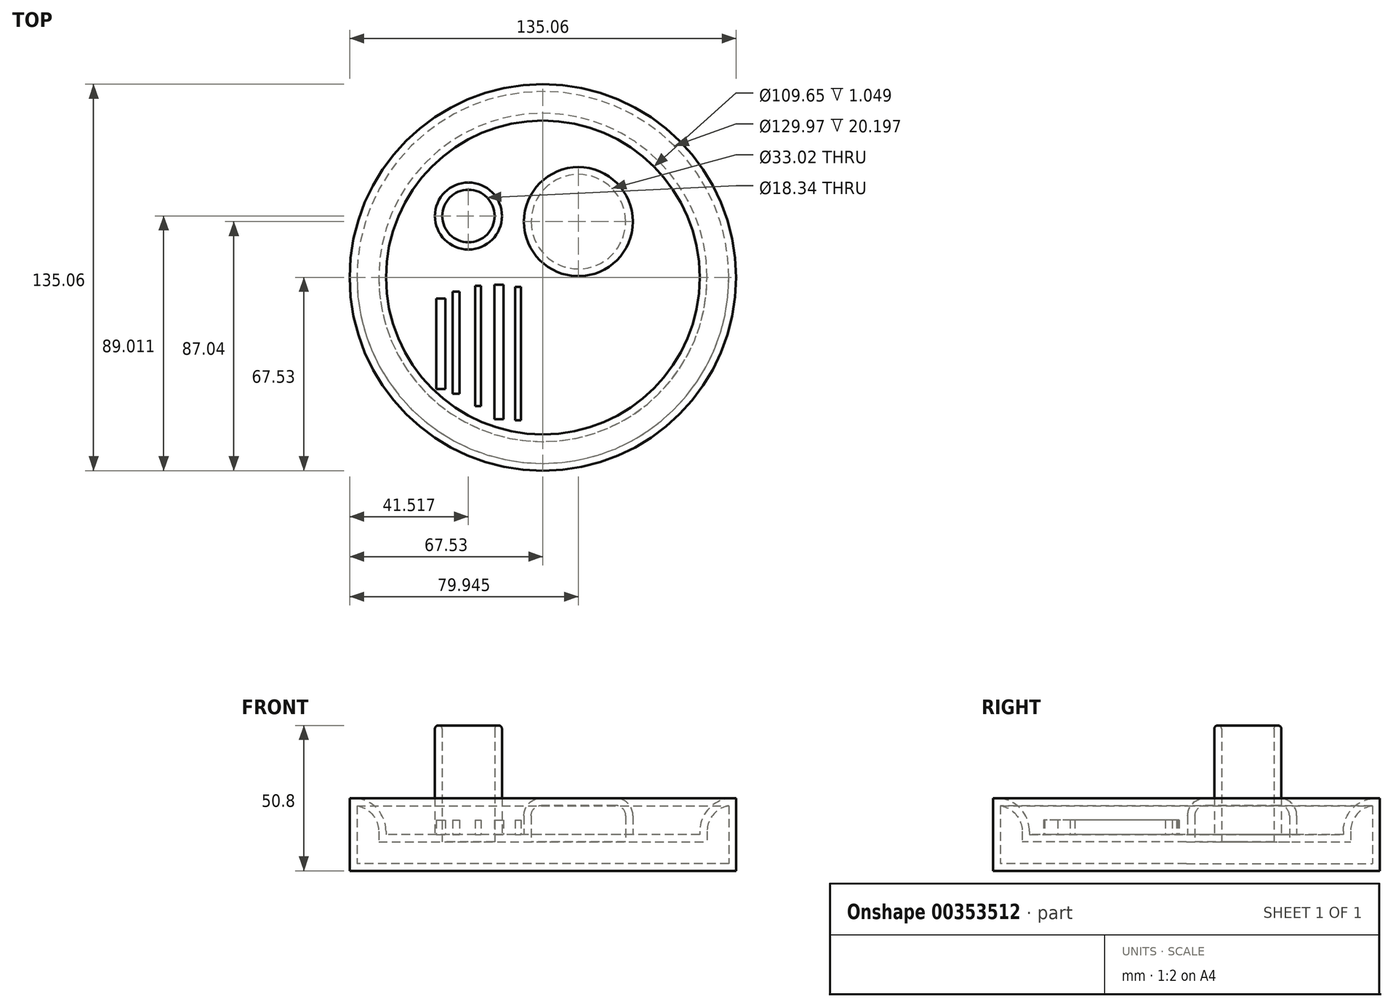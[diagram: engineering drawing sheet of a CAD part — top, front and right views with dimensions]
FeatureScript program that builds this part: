
annotation { "Feature Type Name" : "Feature", "Feature Type Description" : "" }
export const myFeature = defineFeature(function(context is Context, id is Id, definition is map)
    precondition{}
    {
        {
            var Q0;
            Q0=qCreatedBy(makeId("Top.planeOp"),FACE);
            var sketch = newSketch(context, id + "F0", { "sketchPlane" : qUnion([Q0])});
            skCircle(sketch, "E0", {"center": v(0, 0) * mm, "radius": 67.53 * mm});
            skSolve(sketch);
        }
        {
            var Q0;
            Q0=makeQuery(id+"F0.imprint","IMPRINT",FACE,{"disambiguationData":[TD([[makeQuery(id+"F0.imprint","IMPRINT",EDGE,{"derivedFrom":sQuery(id+"F0.wireOp",EDGE,"E0")}),1.0]])]});
            extrude(context, id + "F1", {"entities" : qUnion([Q0]), "depth" : 25.4 * mm});
        }
        {
            var Q0;
            Q0=makeQuery(id+"F1.opExtrude","CAP_FACE",FACE,{"disambiguationData":[OSD([sQuery(id+"F0.wireOp",EDGE,"E0")])],"isStart":false});
            shell(context, id + "F2", {"entities" : qUnion([Q0]), "thickness" : 12.7 * mm});
        }
        {
            var Q0;
            {var subQ0=sQuery(id+"F0.wireOp",EDGE,"E0");Q0=makeQuery(id+"F2.opShell","OFFSET_EDGE",EDGE,{"disambiguationData":[OSD([subQ0]),TDD([makeQuery(id+"F1.opExtrude","CAP_EDGE",EDGE,{"disambiguationData":[OSD([subQ0])],"isStart":false})])]});}
            fillet(context, id + "F3", {"entities" : qUnion([Q0]), "radius" : 11.65 * mm, "tangentPropagation" : true, "allowEdgeOverflow" : false});
        }
        {
            var Q0;
            {var subQ0=sQuery(id+"F0.wireOp",EDGE,"E0");Q0=makeQuery(id+"F2.opShell","OFFSET_FACE",FACE,{"disambiguationData":[OSD([subQ0]),TDD([makeQuery(id+"F1.opExtrude","CAP_FACE",FACE,{"disambiguationData":[OSD([subQ0])],"isStart":true})])]});}
            var sketch = newSketch(context, id + "F4", { "sketchPlane" : qUnion([Q0])});
            skCircle(sketch, "E1", {"center": v(12.42, 19.5) * mm, "radius": 19.05 * mm});
            skSolve(sketch);
        }
        {
            var Q0;
            Q0=makeQuery(id+"F4.imprint","IMPRINT",FACE,{"disambiguationData":[TD([[makeQuery(id+"F4.imprint","IMPRINT",EDGE,{"derivedFrom":sQuery(id+"F4.wireOp",EDGE,"E1")}),1.0]])]});
            extrude(context, id + "F5", {"entities" : qUnion([Q0]), "operationType" : NewBodyOperationType.ADD, "depth" : 12.7 * mm});
        }
        {
            var Q0;
            Q0=makeQuery(id+"F5.opExtrude","CAP_EDGE",EDGE,{"disambiguationData":[OSD([sQuery(id+"F4.wireOp",EDGE,"E1")])],"isStart":false});
            fillet(context, id + "F6", {"entities" : qUnion([Q0]), "radius" : 6.13 * mm, "tangentPropagation" : true, "allowEdgeOverflow" : false});
        }
        {
            var Q0;
            {var subQ0=sQuery(id+"F0.wireOp",EDGE,"E0");Q0=makeQuery(id+"F2.opShell","OFFSET_FACE",FACE,{"disambiguationData":[OSD([subQ0]),TDD([makeQuery(id+"F1.opExtrude","CAP_FACE",FACE,{"disambiguationData":[OSD([subQ0])],"isStart":true})])]});}
            var sketch = newSketch(context, id + "F7", { "sketchPlane" : qUnion([Q0])});
            skLineSegment(sketch, "E2.bottom", {"start": v(-40.2, -7.1) * mm, "end": v(-42.86, -7.1) * mm});
            skLineSegment(sketch, "E2.top", {"start": v(-40.2, -34.18) * mm, "end": v(-42.86, -34.18) * mm});
            skLineSegment(sketch, "E2.left", {"start": v(-40.2, -7.1) * mm, "end": v(-40.2, -34.18) * mm});
            skLineSegment(sketch, "E2.right", {"start": v(-42.86, -7.1) * mm, "end": v(-42.86, -34.18) * mm});
            skLineSegment(sketch, "E3.bottom", {"start": v(-31.53, -4.93) * mm, "end": v(-29.17, -4.93) * mm});
            skLineSegment(sketch, "E3.top", {"start": v(-31.53, -40.6) * mm, "end": v(-29.17, -40.6) * mm});
            skLineSegment(sketch, "E3.left", {"start": v(-31.53, -4.93) * mm, "end": v(-31.53, -40.6) * mm});
            skLineSegment(sketch, "E3.right", {"start": v(-29.17, -4.93) * mm, "end": v(-29.17, -40.6) * mm});
            skLineSegment(sketch, "E4.bottom", {"start": v(-37.25, -7.3) * mm, "end": v(-34.1, -7.3) * mm});
            skLineSegment(sketch, "E4.top", {"start": v(-37.25, -39.02) * mm, "end": v(-34.1, -39.02) * mm});
            skLineSegment(sketch, "E4.left", {"start": v(-37.25, -7.3) * mm, "end": v(-37.25, -39.02) * mm});
            skLineSegment(sketch, "E4.right", {"start": v(-34.1, -7.3) * mm, "end": v(-34.1, -39.02) * mm});
            skLineSegment(sketch, "E5.bottom", {"start": v(-23.65, -2.96) * mm, "end": v(-21.68, -2.96) * mm});
            skLineSegment(sketch, "E5.top", {"start": v(-23.65, -44.93) * mm, "end": v(-21.68, -44.93) * mm});
            skLineSegment(sketch, "E5.left", {"start": v(-23.65, -2.96) * mm, "end": v(-23.65, -44.93) * mm});
            skLineSegment(sketch, "E5.right", {"start": v(-21.68, -2.96) * mm, "end": v(-21.68, -44.93) * mm});
            skLineSegment(sketch, "E6.bottom", {"start": v(-16.95, -2.56) * mm, "end": v(-13.8, -2.56) * mm});
            skLineSegment(sketch, "E6.top", {"start": v(-16.95, -49.46) * mm, "end": v(-13.8, -49.46) * mm});
            skLineSegment(sketch, "E6.left", {"start": v(-16.95, -2.56) * mm, "end": v(-16.95, -49.46) * mm});
            skLineSegment(sketch, "E6.right", {"start": v(-13.8, -2.56) * mm, "end": v(-13.8, -49.46) * mm});
            skLineSegment(sketch, "E7.bottom", {"start": v(-9.66, -3.35) * mm, "end": v(-7.69, -3.35) * mm});
            skLineSegment(sketch, "E7.top", {"start": v(-9.66, -49.86) * mm, "end": v(-7.69, -49.86) * mm});
            skLineSegment(sketch, "E7.left", {"start": v(-9.66, -3.35) * mm, "end": v(-9.66, -49.86) * mm});
            skLineSegment(sketch, "E7.right", {"start": v(-7.69, -3.35) * mm, "end": v(-7.69, -49.86) * mm});
            skSolve(sketch);
        }
        {
            var Q0;
            Q0=makeQuery(id+"F7.imprint","IMPRINT",FACE,{"disambiguationData":[TD([[makeQuery(id+"F7.imprint","IMPRINT",EDGE,{"derivedFrom":sQuery(id+"F7.wireOp",EDGE,"E2.bottom")}),-1.0]])]});
            var sketch = newSketch(context, id + "F8", { "sketchPlane" : qUnion([Q0])});
            skCircle(sketch, "E8", {"center": v(-26.01, 21.48) * mm, "radius": 11.7 * mm});
            skSolve(sketch);
        }
        {
            var Q0;
            Q0 = qSketchRegion(id + "F8", true);
            extrude(context, id + "F9", {"entities" : qUnion([Q0]), "operationType" : NewBodyOperationType.ADD, "depth" : 38.1 * mm});
        }
        {
            var Q0;
            Q0=makeQuery(id+"F9.opExtrude","CAP_FACE",FACE,{"disambiguationData":[OSD([sQuery(id+"F8.wireOp",EDGE,"E8")])],"isStart":false});
            shell(context, id + "F10", {"entities" : qUnion([Q0]), "thickness" : 2.54 * mm});
        }
        {
            var Q0;
            Q0=makeQuery(id+"F9.opExtrude","CAP_FACE",FACE,{"disambiguationData":[OSD([sQuery(id+"F8.wireOp",EDGE,"E8")])],"isStart":false});
            fillet(context, id + "F11", {"entities" : qUnion([Q0]), "radius" : 1.23 * mm, "tangentPropagation" : true, "allowEdgeOverflow" : false});
        }
        {
            var Q0;
            Q0=makeQuery(id+"F7.imprint","IMPRINT",FACE,{"disambiguationData":[TD([[makeQuery(id+"F7.imprint","IMPRINT",EDGE,{"derivedFrom":sQuery(id+"F7.wireOp",EDGE,"E4.bottom")}),-1.0]])]});
            var Q1;
            Q1=makeQuery(id+"F7.imprint","IMPRINT",FACE,{"disambiguationData":[TD([[makeQuery(id+"F7.imprint","IMPRINT",EDGE,{"derivedFrom":sQuery(id+"F7.wireOp",EDGE,"E3.bottom")}),-1.0]])]});
            var Q2;
            Q2=makeQuery(id+"F7.imprint","IMPRINT",FACE,{"disambiguationData":[TD([[makeQuery(id+"F7.imprint","IMPRINT",EDGE,{"derivedFrom":sQuery(id+"F7.wireOp",EDGE,"E5.bottom")}),-1.0]])]});
            var Q3;
            Q3=makeQuery(id+"F7.imprint","IMPRINT",FACE,{"disambiguationData":[TD([[makeQuery(id+"F7.imprint","IMPRINT",EDGE,{"derivedFrom":sQuery(id+"F7.wireOp",EDGE,"E6.bottom")}),-1.0]])]});
            var Q4;
            Q4=makeQuery(id+"F7.imprint","IMPRINT",FACE,{"disambiguationData":[TD([[makeQuery(id+"F7.imprint","IMPRINT",EDGE,{"derivedFrom":sQuery(id+"F7.wireOp",EDGE,"E7.bottom")}),-1.0]])]});
            extrude(context, id + "F12", {"entities" : qUnion([Q0, Q1, Q2, Q3, Q4]), "operationType" : NewBodyOperationType.ADD, "depth" : 5.08 * mm});
        }
    });
